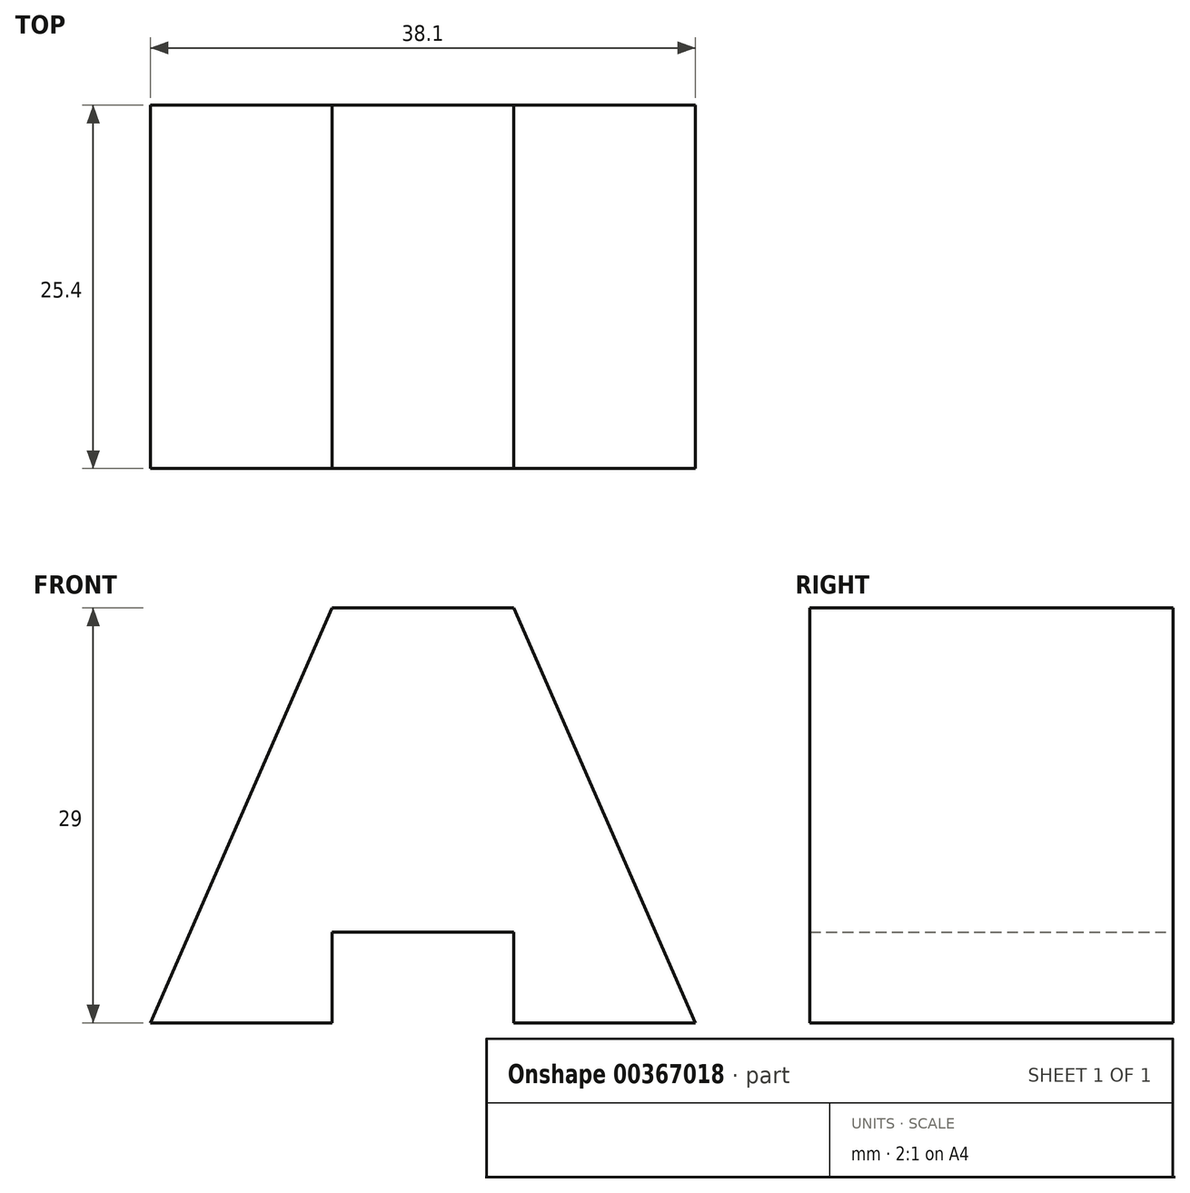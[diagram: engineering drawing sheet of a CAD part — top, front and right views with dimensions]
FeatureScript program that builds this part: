
annotation { "Feature Type Name" : "Feature", "Feature Type Description" : "" }
export const myFeature = defineFeature(function(context is Context, id is Id, definition is map)
    precondition{}
    {
        {
            var Q0;
            Q0=qCreatedBy(makeId("Front.planeOp"),FACE);
            var sketch = newSketch(context, id + "F0", { "sketchPlane" : qUnion([Q0])});
            skLineSegment(sketch, "E0", {"start": v(0, 0) * mm, "end": v(12.7, 0) * mm});
            skLineSegment(sketch, "E1", {"start": v(12.7, 0) * mm, "end": v(12.7, 6.35) * mm});
            skLineSegment(sketch, "E2", {"start": v(12.7, 6.35) * mm, "end": v(25.4, 6.35) * mm});
            skLineSegment(sketch, "E3", {"start": v(25.4, 6.35) * mm, "end": v(25.4, 0) * mm});
            skLineSegment(sketch, "E4", {"start": v(25.4, 0) * mm, "end": v(38.1, 0) * mm});
            skLineSegment(sketch, "E5", {"start": v(38.1, 0) * mm, "end": v(25.4, 29) * mm});
            skLineSegment(sketch, "E6", {"start": v(25.4, 29) * mm, "end": v(12.7, 29) * mm});
            skLineSegment(sketch, "E7", {"start": v(12.7, 29) * mm, "end": v(0, 0) * mm});
            skSolve(sketch);
        }
        {
            var Q0;
            Q0=makeQuery(id+"F0.imprint","IMPRINT",FACE,{"disambiguationData":[TD([[makeQuery(id+"F0.imprint","IMPRINT",EDGE,{"derivedFrom":sQuery(id+"F0.wireOp",EDGE,"E0")}),1.0]])]});
            extrude(context, id + "F1", {"entities" : qUnion([Q0]), "depth" : 25.4 * mm});
        }
    });
